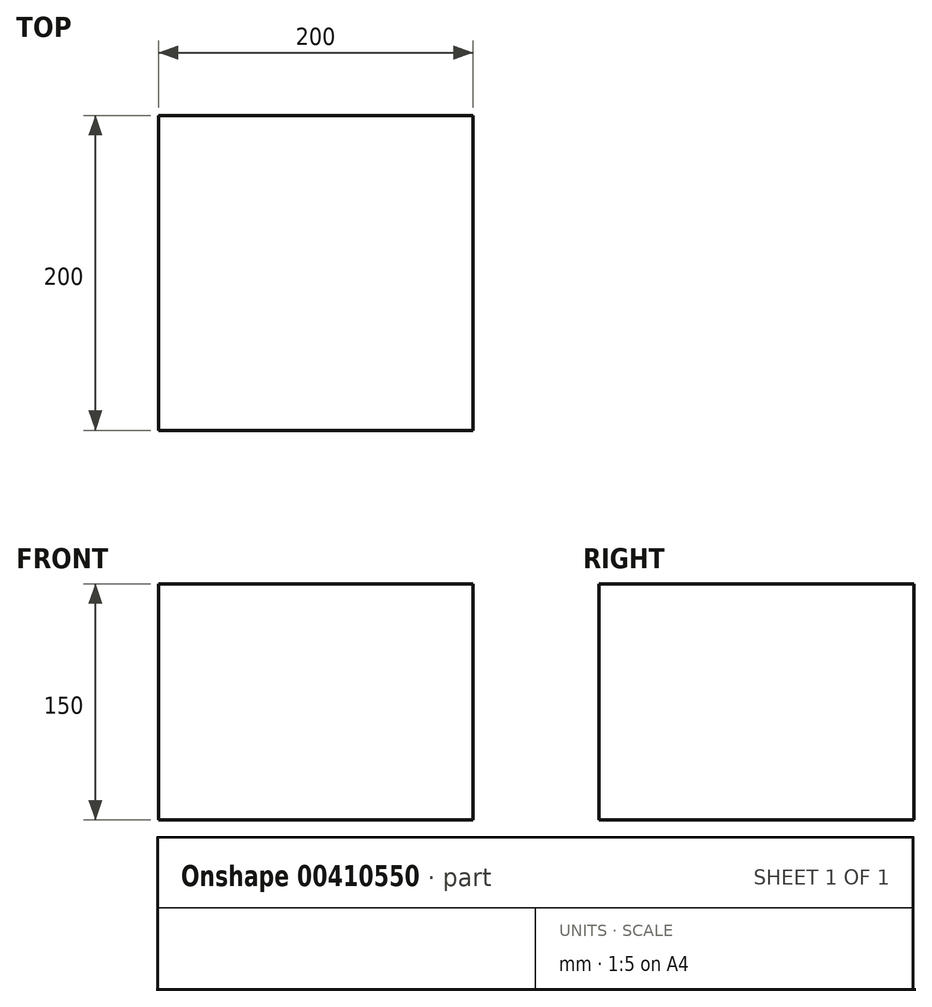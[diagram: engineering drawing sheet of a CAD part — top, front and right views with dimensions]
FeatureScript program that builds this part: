
annotation { "Feature Type Name" : "Feature", "Feature Type Description" : "" }
export const myFeature = defineFeature(function(context is Context, id is Id, definition is map)
    precondition{}
    {
        {
            var Q0;
            Q0=qCreatedBy(makeId("Top.planeOp"),FACE);
            var sketch = newSketch(context, id + "F0", { "sketchPlane" : qUnion([Q0])});
            skLineSegment(sketch, "E0.bottom", {"start": v(222.94, 209.04) * mm, "end": v(22.94, 209.04) * mm});
            skLineSegment(sketch, "E0.top", {"start": v(222.94, 9.04) * mm, "end": v(22.94, 9.04) * mm});
            skLineSegment(sketch, "E0.left", {"start": v(222.94, 209.04) * mm, "end": v(222.94, 9.04) * mm});
            skLineSegment(sketch, "E0.right", {"start": v(22.94, 209.04) * mm, "end": v(22.94, 9.04) * mm});
            skSolve(sketch);
        }
        {
            var Q0;
            Q0 = qSketchRegion(id + "F0", true);
            extrude(context, id + "F1", {"entities" : qUnion([Q0]), "depth" : 150 * mm});
        }
    });
